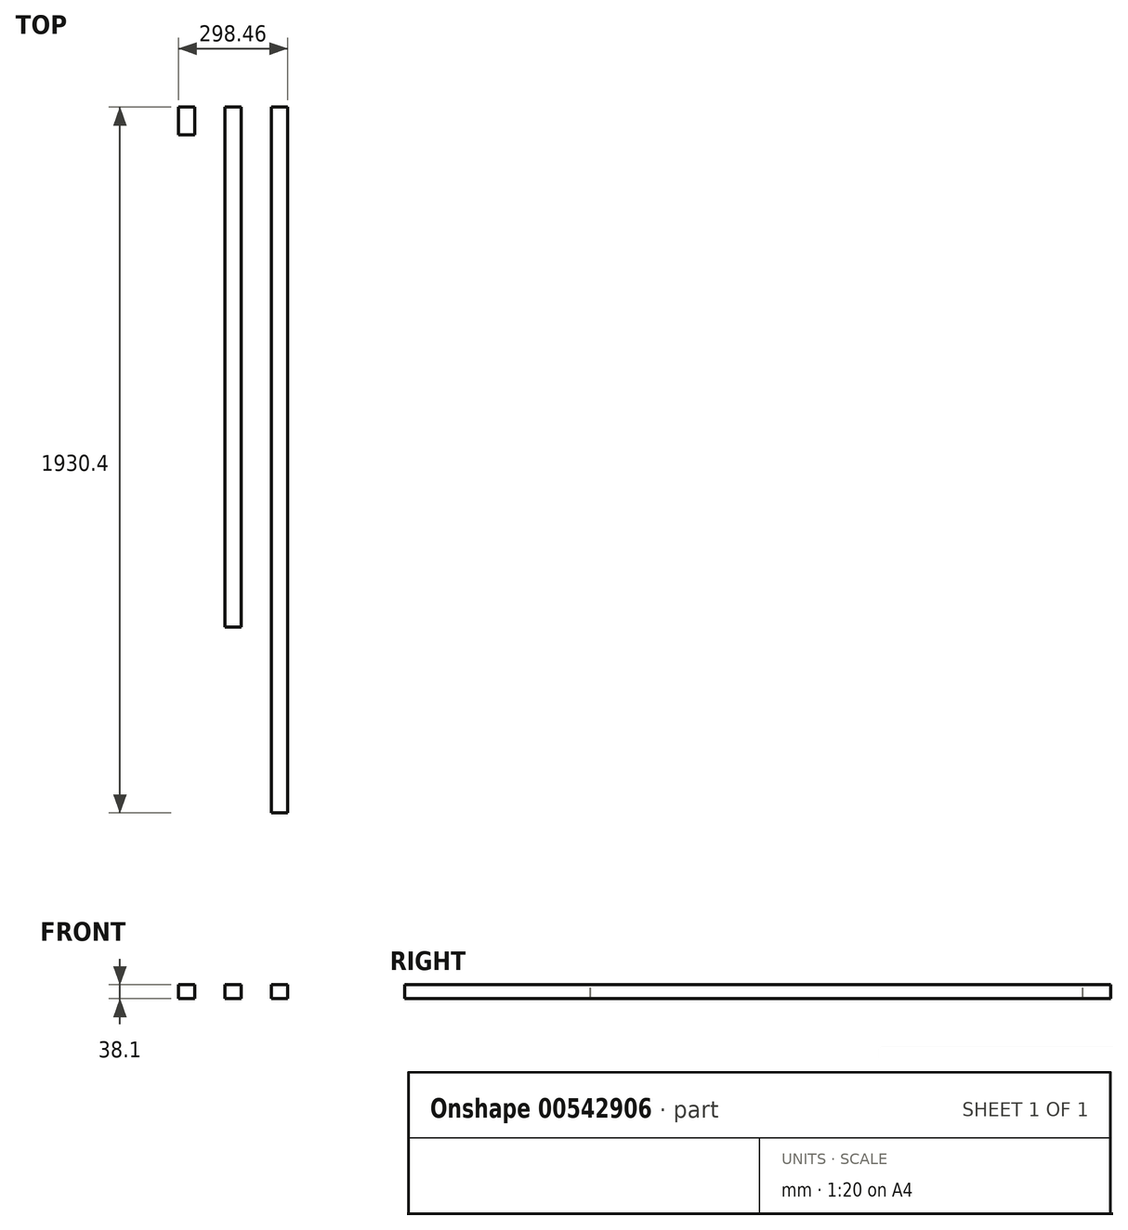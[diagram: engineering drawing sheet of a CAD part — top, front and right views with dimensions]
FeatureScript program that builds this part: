
annotation { "Feature Type Name" : "Feature", "Feature Type Description" : "" }
export const myFeature = defineFeature(function(context is Context, id is Id, definition is map)
    precondition{}
    {
        {
            var Q0;
            Q0=qCreatedBy(makeId("Front.planeOp"),FACE);
            var sketch = newSketch(context, id + "F0", { "sketchPlane" : qUnion([Q0])});
            skLineSegment(sketch, "E0.bottom", {"start": v(22.23, -19.05) * mm, "end": v(-22.23, -19.05) * mm});
            skLineSegment(sketch, "E0.top", {"start": v(22.23, 19.05) * mm, "end": v(-22.23, 19.05) * mm});
            skLineSegment(sketch, "E0.left", {"start": v(22.23, -19.05) * mm, "end": v(22.23, 19.05) * mm});
            skLineSegment(sketch, "E0.right", {"start": v(-22.23, -19.05) * mm, "end": v(-22.23, 19.05) * mm});
            skPoint(sketch, "E0.middle", {"position": v(0, 0) * mm});
            skSolve(sketch);
        }
        {
            var Q0;
            Q0=qSketchRegion(id+"F0",true);
            extrude(context, id + "F1", {"entities" : qUnion([Q0]), "depth" : 76.2 * mm});
        }
        {
            var Q0;
            Q0=makeQuery(id+"F1.opExtrude","SWEPT_BODY",BODY,{"disambiguationData":[OSD([sQuery(id+"F0.wireOp",EDGE,"E0.bottom"),sQuery(id+"F0.wireOp",EDGE,"E0.top"),sQuery(id+"F0.wireOp",EDGE,"E0.left"),sQuery(id+"F0.wireOp",EDGE,"E0.right")])]});
            transform(context, id + "F2", {"entities" : qUnion([Q0]), "transformType" : TransformType.TRANSLATION_3D, "dx" : 127 * mm, "dy" : 0 * mm, "dz" : 0 * mm, "makeCopy" : true});
        }
        {
            var Q0;
            Q0=makeQuery(id+"F2.opPattern","COPY",FACE,{"derivedFrom":makeQuery(id+"F1.opExtrude","CAP_FACE",FACE,{"disambiguationData":[OSD([sQuery(id+"F0.wireOp",EDGE,"E0.bottom"),sQuery(id+"F0.wireOp",EDGE,"E0.top"),sQuery(id+"F0.wireOp",EDGE,"E0.left"),sQuery(id+"F0.wireOp",EDGE,"E0.right")])],"isStart":false}),"instanceName":"1"});
            extrude(context, id + "F3", {"entities" : qUnion([Q0]), "operationType" : NewBodyOperationType.ADD, "depth" : 1346.2 * mm});
        }
        {
            var Q0;
            Q0=makeQuery(id+"F1.opExtrude","SWEPT_BODY",BODY,{"disambiguationData":[OSD([sQuery(id+"F0.wireOp",EDGE,"E0.bottom"),sQuery(id+"F0.wireOp",EDGE,"E0.top"),sQuery(id+"F0.wireOp",EDGE,"E0.left"),sQuery(id+"F0.wireOp",EDGE,"E0.right")])]});
            transform(context, id + "F4", {"entities" : qUnion([Q0]), "transformType" : TransformType.TRANSLATION_3D, "dx" : 254 * mm, "dy" : 0 * mm, "dz" : 0 * mm, "makeCopy" : true});
        }
        {
            var Q0;
            Q0=makeQuery(id+"F4.opPattern","COPY",FACE,{"derivedFrom":makeQuery(id+"F1.opExtrude","CAP_FACE",FACE,{"disambiguationData":[OSD([sQuery(id+"F0.wireOp",EDGE,"E0.bottom"),sQuery(id+"F0.wireOp",EDGE,"E0.top"),sQuery(id+"F0.wireOp",EDGE,"E0.left"),sQuery(id+"F0.wireOp",EDGE,"E0.right")])],"isStart":false}),"instanceName":"1"});
            extrude(context, id + "F5", {"entities" : qUnion([Q0]), "operationType" : NewBodyOperationType.ADD, "depth" : 1854.2 * mm});
        }
    });
